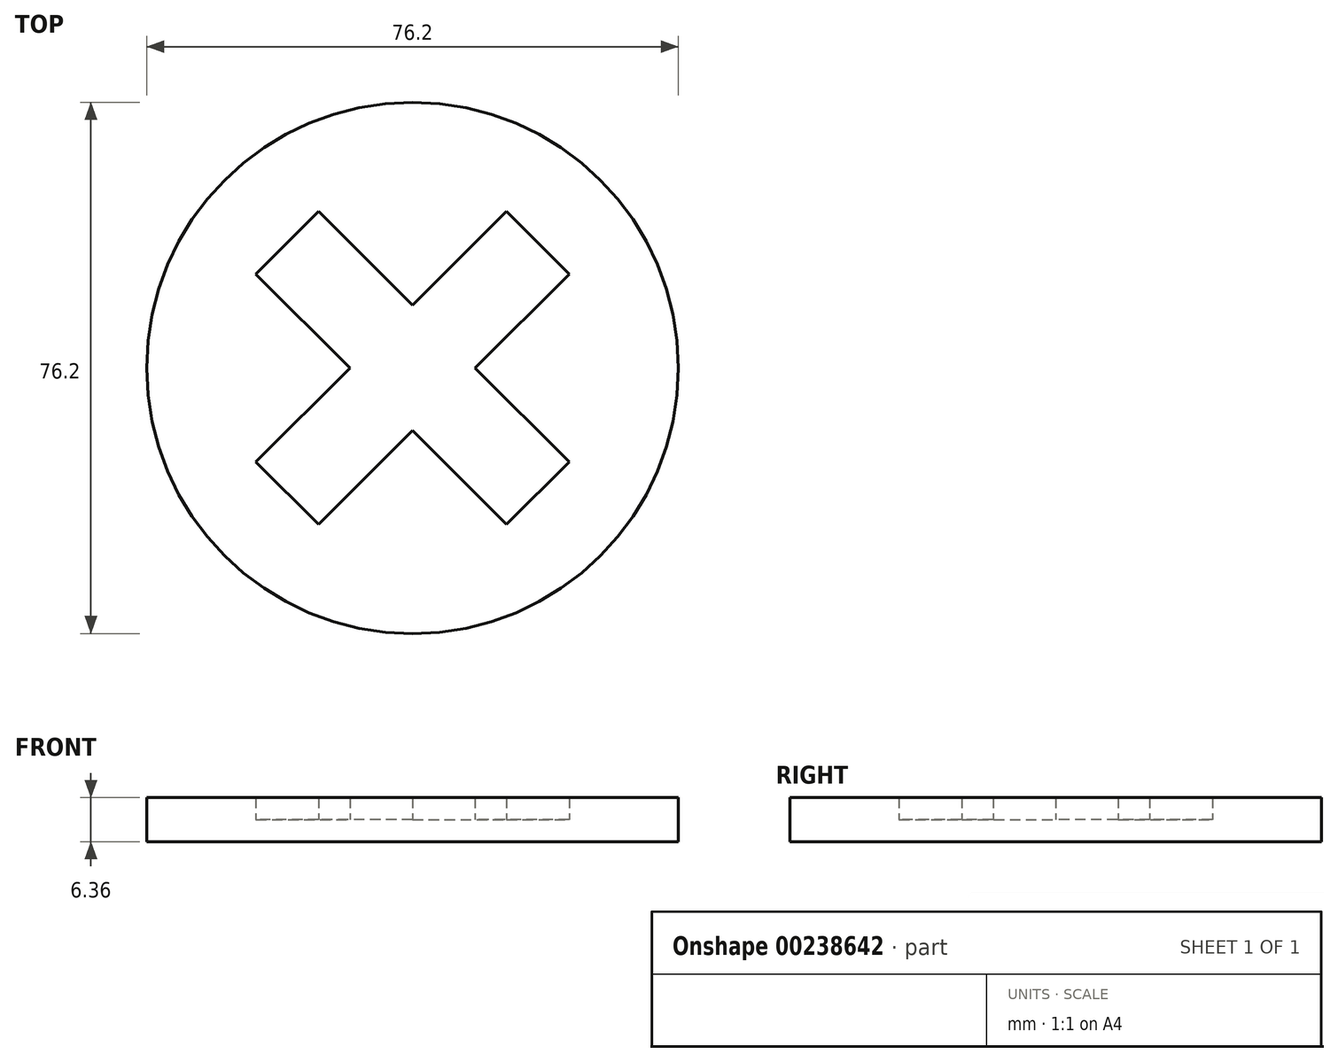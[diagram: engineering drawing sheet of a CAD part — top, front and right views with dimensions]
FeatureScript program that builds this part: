
annotation { "Feature Type Name" : "Feature", "Feature Type Description" : "" }
export const myFeature = defineFeature(function(context is Context, id is Id, definition is map)
    precondition{}
    {
        {
            var Q0;
            Q0=qCreatedBy(makeId("Top.planeOp"),FACE);
            var sketch = newSketch(context, id + "F0", { "sketchPlane" : qUnion([Q0])});
            skCircle(sketch, "E0", {"center": v(0, 0) * mm, "radius": 38.1 * mm});
            skSolve(sketch);
        }
        {
            var Q0;
            Q0=makeQuery(id+"F0.imprint","IMPRINT",FACE,{"disambiguationData":[TD([[makeQuery(id+"F0.imprint","IMPRINT",EDGE,{"derivedFrom":sQuery(id+"F0.wireOp",EDGE,"E0")}),1.0]])]});
            extrude(context, id + "F1", {"entities" : qUnion([Q0]), "depth" : 3.17 * mm});
        }
        {
            var Q0;
            Q0 = qSketchRegion(id + "F0", true);
            extrude(context, id + "F2", {"entities" : qUnion([Q0]), "oppositeDirection" : true, "depth" : 3.17 * mm});
        }
        {
            var Q0;
            Q0=makeQuery(id+"F1.opExtrude","CAP_FACE",FACE,{"disambiguationData":[OSD([sQuery(id+"F0.wireOp",EDGE,"E0")])],"isStart":false});
            var sketch = newSketch(context, id + "F3", { "sketchPlane" : qUnion([Q0])});
            skCircle(sketch, "E1", {"center": v(0, 0) * mm, "radius": 31.75 * mm});
            skSolve(sketch);
        }
        {
            var Q0;
            Q0=makeQuery(id+"F3.imprint","IMPRINT",FACE,{"disambiguationData":[TD([[makeQuery(id+"F3.imprint","IMPRINT",EDGE,{"derivedFrom":sQuery(id+"F3.wireOp",EDGE,"E1")}),-1.0]])]});
            extrude(context, id + "F4", {"entities" : qUnion([Q0]), "operationType" : NewBodyOperationType.REMOVE, "endBound" : BoundingType.UP_TO_NEXT, "oppositeDirection" : true, "depth" : 25.4 * mm});
        }
        {
            var Q0;
            Q0=makeQuery(id+"F0.imprint","IMPRINT",FACE,{"disambiguationData":[TD([[makeQuery(id+"F0.imprint","IMPRINT",EDGE,{"derivedFrom":sQuery(id+"F0.wireOp",EDGE,"E0")}),1.0]])]});
            var sketch = newSketch(context, id + "F5", { "sketchPlane" : qUnion([Q0])});
            skCircle(sketch, "E2.0", {"center": v(0, 0) * mm, "radius": 31.75 * mm});
            skSolve(sketch);
        }
        {
            var Q0;
            Q0=makeQuery(id+"F5.imprint","IMPRINT",FACE,{"disambiguationData":[TD([[makeQuery(id+"F5.imprint","IMPRINT",EDGE,{"derivedFrom":sQuery(id+"F5.wireOp",EDGE,"E2.0")}),-1.0]])]});
            var Q1;
            Q1=makeQuery(id+"F1.opExtrude","CAP_FACE",FACE,{"disambiguationData":[OSD([sQuery(id+"F0.wireOp",EDGE,"E0")])],"isStart":false});
            extrude(context, id + "F6", {"entities" : qUnion([Q0]), "operationType" : NewBodyOperationType.ADD, "endBound" : BoundingType.UP_TO_SURFACE, "endBoundEntityFace" : qUnion([Q1]), "depth" : 25.4 * mm});
        }
        {
            var Q0;
            Q0=makeQuery(id+"F2.opExtrude","CAP_FACE",FACE,{"disambiguationData":[OSD([sQuery(id+"F0.wireOp",EDGE,"E0")])],"isStart":false});
            var sketch = newSketch(context, id + "F7", { "sketchPlane" : qUnion([Q0])});
            skLineSegment(sketch, "E3", {"start": v(0, 8.98) * mm, "end": v(13.47, 22.45) * mm});
            skLineSegment(sketch, "E4", {"start": v(13.47, 22.45) * mm, "end": v(22.45, 13.47) * mm});
            skLineSegment(sketch, "E5", {"start": v(22.45, 13.47) * mm, "end": v(8.98, 0) * mm});
            skLineSegment(sketch, "E6.MirrorCS", {"start": v(0, 8.98) * mm, "end": v(-13.47, 22.45) * mm});
            skLineSegment(sketch, "E7.MirrorCS", {"start": v(-22.45, 13.47) * mm, "end": v(-8.98, 0) * mm});
            skLineSegment(sketch, "E8.MirrorCS", {"start": v(-13.47, 22.45) * mm, "end": v(-22.45, 13.47) * mm});
            skLineSegment(sketch, "E9.MirrorCS", {"start": v(0, -8.98) * mm, "end": v(-13.47, -22.45) * mm});
            skLineSegment(sketch, "E10.MirrorCS", {"start": v(-22.45, -13.47) * mm, "end": v(-8.98, 0) * mm});
            skLineSegment(sketch, "E11.MirrorCS", {"start": v(22.45, -13.47) * mm, "end": v(8.98, 0) * mm});
            skLineSegment(sketch, "E12.MirrorCS", {"start": v(0, -8.98) * mm, "end": v(13.47, -22.45) * mm});
            skLineSegment(sketch, "E13.MirrorCS", {"start": v(13.47, -22.45) * mm, "end": v(22.45, -13.47) * mm});
            skLineSegment(sketch, "E14.MirrorCS", {"start": v(-13.47, -22.45) * mm, "end": v(-22.45, -13.47) * mm});
            skSolve(sketch);
        }
        {
            var Q0;
            Q0=makeQuery(id+"F7.imprint","IMPRINT",FACE,{"disambiguationData":[TD([[makeQuery(id+"F7.imprint","IMPRINT",EDGE,{"derivedFrom":sQuery(id+"F7.wireOp",EDGE,"E3")}),-1.0]])]});
            extrude(context, id + "F8", {"entities" : qUnion([Q0]), "operationType" : NewBodyOperationType.REMOVE, "endBound" : BoundingType.UP_TO_NEXT, "oppositeDirection" : true, "depth" : 25.4 * mm});
        }
        {
            var Q0;
            Q0=makeQuery(id+"F0.imprint","IMPRINT",FACE,{"disambiguationData":[TD([[makeQuery(id+"F0.imprint","IMPRINT",EDGE,{"derivedFrom":sQuery(id+"F0.wireOp",EDGE,"E0")}),1.0]])]});
            var sketch = newSketch(context, id + "F9", { "sketchPlane" : qUnion([Q0])});
            skLineSegment(sketch, "E15.0", {"start": v(0, -8.98) * mm, "end": v(-13.47, -22.45) * mm});
            skLineSegment(sketch, "E16.0", {"start": v(-13.47, -22.45) * mm, "end": v(-22.45, -13.47) * mm});
            skLineSegment(sketch, "E17.0", {"start": v(-22.45, -13.47) * mm, "end": v(-8.98, 0) * mm});
            skLineSegment(sketch, "E18.0", {"start": v(-22.45, 13.47) * mm, "end": v(-8.98, 0) * mm});
            skLineSegment(sketch, "E19.0", {"start": v(-13.47, 22.45) * mm, "end": v(-22.45, 13.47) * mm});
            skLineSegment(sketch, "E20.0", {"start": v(0, 8.98) * mm, "end": v(-13.47, 22.45) * mm});
            skLineSegment(sketch, "E21.0", {"start": v(0, 8.98) * mm, "end": v(13.47, 22.45) * mm});
            skLineSegment(sketch, "E22.0", {"start": v(22.45, 13.47) * mm, "end": v(8.98, 0) * mm});
            skLineSegment(sketch, "E23.0", {"start": v(13.47, 22.45) * mm, "end": v(22.45, 13.47) * mm});
            skLineSegment(sketch, "E24.0", {"start": v(22.45, -13.47) * mm, "end": v(8.98, 0) * mm});
            skLineSegment(sketch, "E25.0", {"start": v(0, -8.98) * mm, "end": v(13.47, -22.45) * mm});
            skLineSegment(sketch, "E26.0", {"start": v(13.47, -22.45) * mm, "end": v(22.45, -13.47) * mm});
            skSolve(sketch);
        }
        {
            var Q0;
            Q0 = qSketchRegion(id + "F9", true);
            var Q1;
            Q1=makeQuery(id+"F2.opExtrude","CAP_FACE",FACE,{"disambiguationData":[OSD([sQuery(id+"F0.wireOp",EDGE,"E0")])],"isStart":false});
            extrude(context, id + "F10", {"entities" : qUnion([Q0]), "operationType" : NewBodyOperationType.ADD, "endBound" : BoundingType.UP_TO_SURFACE, "oppositeDirection" : true, "endBoundEntityFace" : qUnion([Q1]), "depth" : 25.4 * mm});
        }
    });
